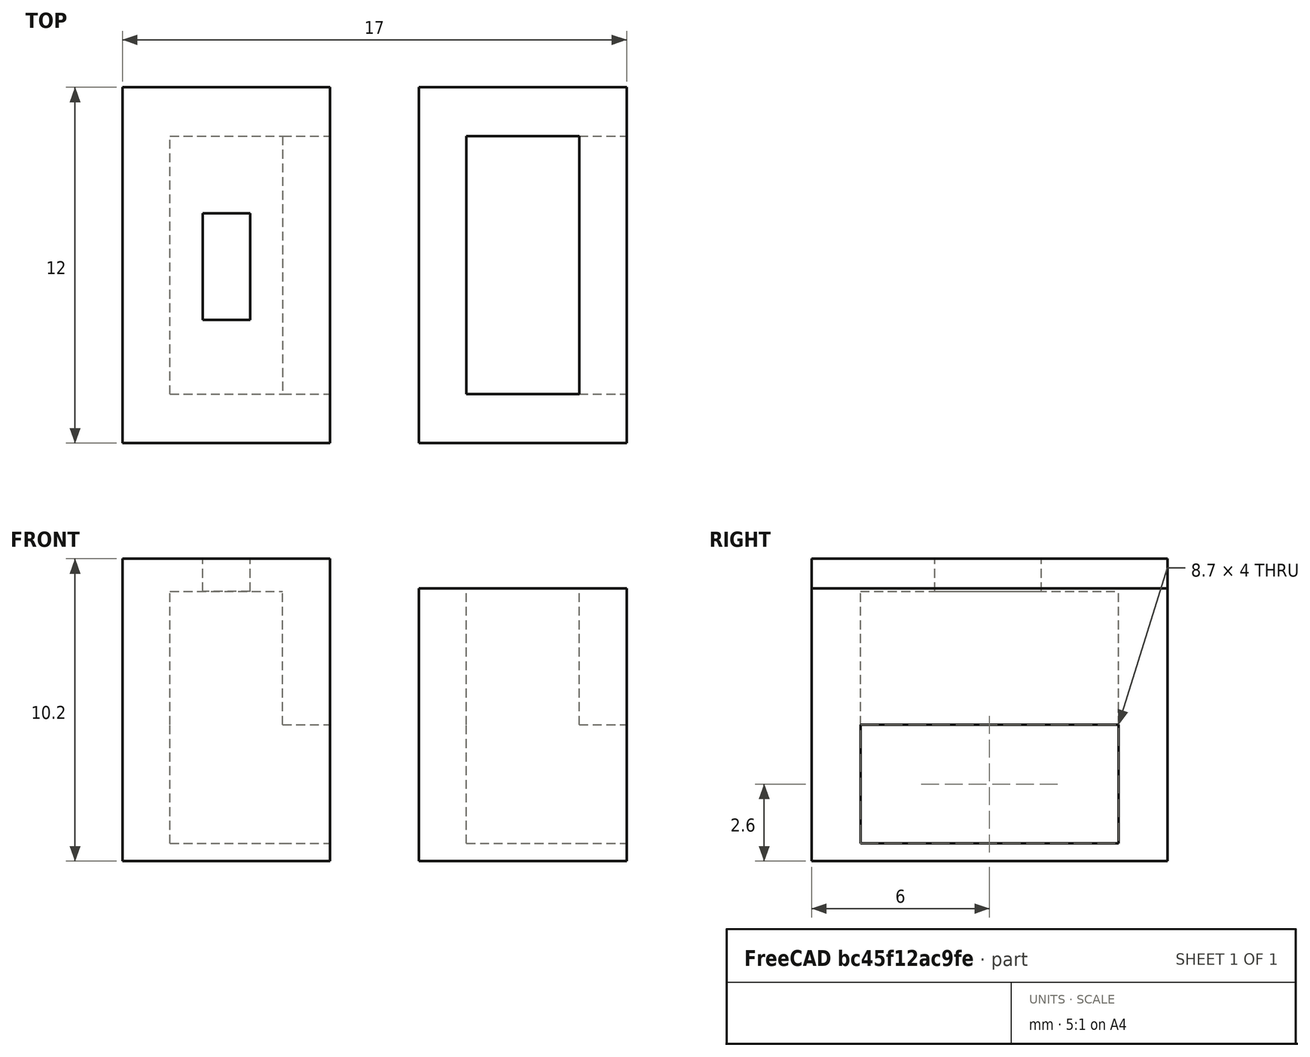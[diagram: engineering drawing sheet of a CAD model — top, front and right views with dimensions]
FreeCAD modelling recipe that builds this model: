
FCSTD DOCUMENT  (FreeCAD 0.20R29177 +426 (Git))
Label: interruptorHolder
License: All rights reserved
LicenseURL: http://en.wikipedia.org/wiki/All_rights_reserved
objects: Part::Box×8, Part::MultiFuse×2, Part::Cut×2
note: 12 computed .brp shape members not serialized (recipe doc carries the construction recipe); baked Part::Feature solids carry a one-line shape summary decoded from their .brp

FEATURE [Part::Box] Box  label="Cube"
  AttacherType = Attacher::AttachEngine3D
  Height = 9.5
  Length = 3.8
  Width = 8.7
FEATURE [Part::Box] Box001  label="Cube001"
  AttacherType = Attacher::AttachEngine3D
  Height = 9.2
  Length = 7
  Placement = pos=(-1.6,-1.65,-0.6) rot=(0,0,1;0rad)
  Width = 12
FEATURE [Part::Box] Box002  label="Cube002"
  AttacherType = Attacher::AttachEngine3D
  Height = 4
  Length = 5.8
  Width = 8.7
FEATURE [Part::Box] Box003  label="Cube003"
  AttacherType = Attacher::AttachEngine3D
  Height = 8.5
  Length = 1.6
  Placement = pos=(1.1,2.5,1) rot=(0,0,1;0rad)
  Width = 3.6
FEATURE [Part::MultiFuse] Fusion
  Shapes = -> [Box,Box002,Box003]
FEATURE [Part::Cut] Cut
  Base = -> Box001
  Tool = -> Fusion
FEATURE [Part::Box] Box004  label="Cube004"
  AttacherType = Attacher::AttachEngine3D
  Height = 8.5
  Length = 3.8
  Width = 8.7
FEATURE [Part::Box] Box005  label="Cube005"
  AttacherType = Attacher::AttachEngine3D
  Height = 10.2
  Length = 7
  Placement = pos=(-1.6,-1.65,-0.6) rot=(0,0,1;0rad)
  Width = 12
FEATURE [Part::Box] Box006  label="Cube006"
  AttacherType = Attacher::AttachEngine3D
  Height = 4
  Length = 5.8
  Width = 8.7
FEATURE [Part::Box] Box007  label="Cube007"
  AttacherType = Attacher::AttachEngine3D
  Height = 10
  Length = 1.6
  Placement = pos=(1.1,2.5,1) rot=(0,0,1;0rad)
  Width = 3.6
FEATURE [Part::MultiFuse] Fusion001
  Shapes = -> [Box004,Box006,Box007]
FEATURE [Part::Cut] Cut001
  Base = -> Box005
  Placement = pos=(-10,0,0) rot=(0,0,1;0rad)
  Tool = -> Fusion001
